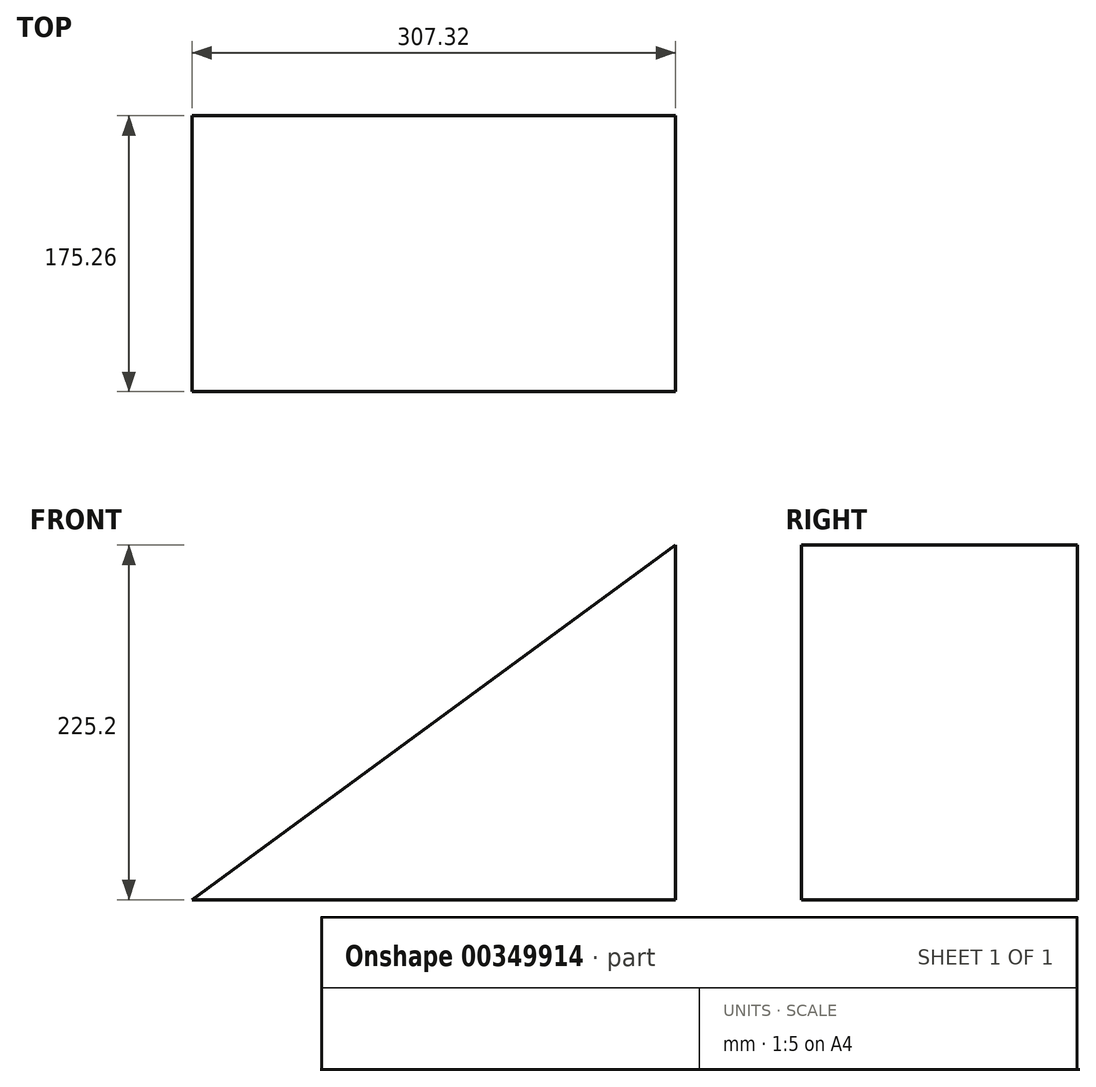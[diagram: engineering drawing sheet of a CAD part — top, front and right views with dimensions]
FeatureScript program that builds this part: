
annotation { "Feature Type Name" : "Feature", "Feature Type Description" : "" }
export const myFeature = defineFeature(function(context is Context, id is Id, definition is map)
    precondition{}
    {
        {
            var Q0;
            Q0=qCreatedBy(makeId("Front.planeOp"),FACE);
            var sketch = newSketch(context, id + "F0", { "sketchPlane" : qUnion([Q0])});
            skLineSegment(sketch, "E0", {"start": v(0, 225.2) * mm, "end": v(-307.32, 0) * mm});
            skLineSegment(sketch, "E1", {"start": v(-307.32, 0) * mm, "end": v(0, 0) * mm});
            skLineSegment(sketch, "E2", {"start": v(0, 0) * mm, "end": v(0, 225.2) * mm});
            skSolve(sketch);
        }
        {
            var Q0;
            Q0 = qSketchRegion(id + "F0", true);
            extrude(context, id + "F1", {"entities" : qUnion([Q0]), "depth" : 175.26 * mm, "offsetDistance" : 25.4 * mm});
        }
    });
